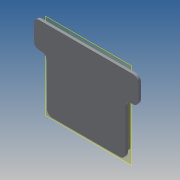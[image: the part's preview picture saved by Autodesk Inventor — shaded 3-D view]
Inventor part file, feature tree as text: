
AUTODESK INVENTOR PART (.ipt)
format: ipt  version: 2013 (Build 170138000, 138)  size: 207,360 bytes
history: native  units: in
note: dims shown in document units (in); Inventor stores cm internally (conversion verified against a paired STEP export)
features: extrude x6, sketch x6, reference x3, plane x1, mirror x1
ambient origin geometry x8: Origin, YZ Plane, XZ Plane, XY Plane, X Axis, Y Axis, Z Axis, Center Point
bodies: Solid1 (feature_tree)
feature tree (17):
  plane  "Work Plane1"
  extrude  "Extrusion1"  Depth=0.3937in TaperAngle=0.0deg
  extrude  "Extrusion2"  Depth=1.9685in
  extrude  "Extrusion3"  Depth=0.0197in
  extrude  "Extrusion4"  Depth=0.1969in TaperAngle=0.0deg
  extrude  "Extrusion5"  Depth=0.1181in TaperAngle=0.0deg
  mirror  "Mirror1"
  extrude  "Extrusion6"  Depth=0.1969in TaperAngle=0.0deg
  sketch  "Sketch1"  dims[d0=0.1969in d1=0.3937in d2=0.0in]
  reference  "Reference1"
  sketch  "Sketch2"  dims[d3=0.9843in d4=1.9685in]
  reference  "Reference2"
  sketch  "Sketch3"  dims[d5=0.1969in d6=0.0in d7=0.0197in]
  sketch  "Sketch4"  dims[d8=0.1969in d9=0.0in d10=0.1969in d11=0.0in]
  reference  "Reference3"
  sketch  "Sketch5"  dims[d12=0.2165in d13=0.1181in d14=0.0in]
  sketch  "Sketch6"  dims[d15=0.5906in d16=0.1969in d17=0.0in]
